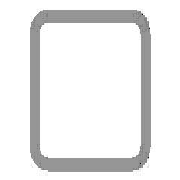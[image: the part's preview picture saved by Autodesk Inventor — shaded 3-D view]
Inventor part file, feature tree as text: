
AUTODESK INVENTOR PART (.ipt)
format: ipt  version: 2025.1 (Build 291241000, 241)  size: 208,384 bytes
history: native  units: mm (DEFAULTED — no unit token found)
features: other x18, sketch x4, extrude x3, plane x1
ambient origin geometry x8: Origin, YZ Plane, XZ Plane, XY Plane, X Axis, Y Axis, Z Axis, Center Point
bodies: Solid1 (feature_tree)
feature tree (26):
  parser-record x1  (decoder bookkeeping rows leaked as tree rows — omitted from the tree; the rows remain in map.json)
  other  "Driven Length"
  other  "Płaszczyzna początkowa"
  other  "Płaszczyzna końcowa"
  extrude  "Bryła"  TaperAngle=0.0deg  [1 undecoded]
  other  "Płaszczyzna konstrukcyjna4"
  other  "Podział1"
  other  "Płaszczyzna konstrukcyjna5"
  other  "Podział2"
  other  "Płaszczyzna konstrukcyjna6"
  other  "Płaszczyzna konstrukcyjna7"
  other  "Płaszczyzna konstrukcyjna8"
  extrude  "Wyciągnięcie proste2"  Depth=4.0mm
  other  "Utwórz kombinację1"
  other  "Płaszczyzna konstrukcyjna9"
  other  "Płaszczyzna konstrukcyjna10"
  other  "Płaszczyzna konstrukcyjna11"
  extrude  "Wyciągnięcie proste3"  Depth=4.0mm
  other  "Utwórz kombinację2"
  sketch  "Sketch3"  dims[d3=1740.0mm d4=0.0mm]
  plane  "Work Plane3"
  sketch  "Sketch4"  dims[d7=4.0mm d10=40.0mm d11=40.0mm d12=3.2mm d13=-20.0mm d14=1720.0mm d15=20.0mm d16=20.0mm d17=90.0deg d18=1740.0mm d19=0.13mm d20=0.0mm d21=0.13mm d22=0.0mm]
  sketch  "Szkic5"
  other  "Bryła2"
  sketch  "Szkic6"
  other  "Bryła3"
note: 1 required parameter value undecoded (feature->parameter linkage not recoverable at this tier; creation-order binding heuristic only, values carry confidence <= 0.55)
